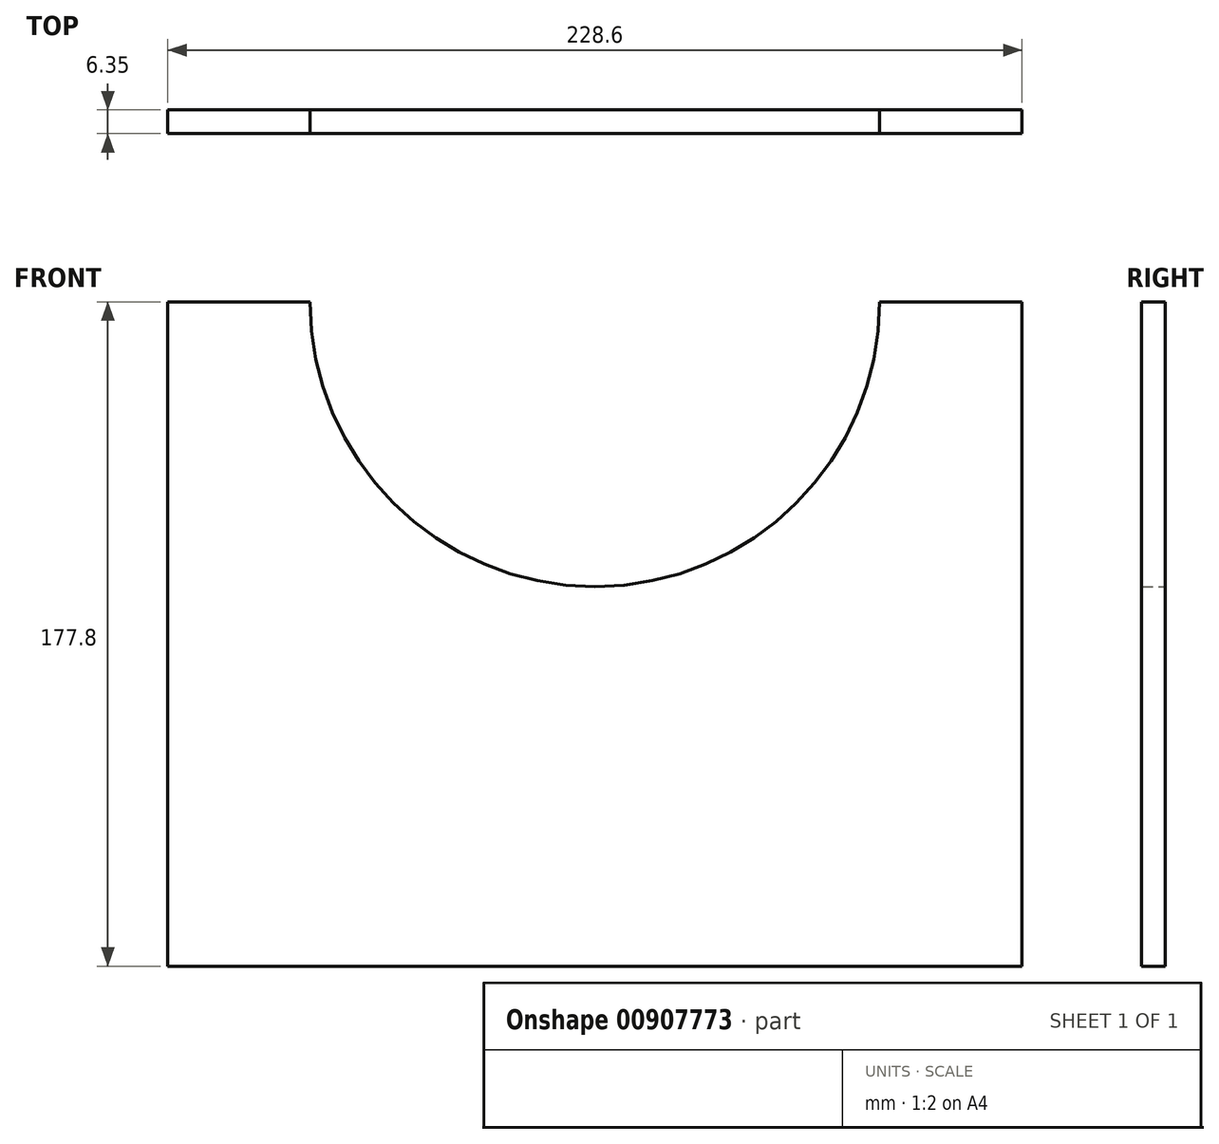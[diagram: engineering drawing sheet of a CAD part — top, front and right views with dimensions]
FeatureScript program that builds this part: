
annotation { "Feature Type Name" : "Feature", "Feature Type Description" : "" }
export const myFeature = defineFeature(function(context is Context, id is Id, definition is map)
    precondition{}
    {
        {
            var Q0;
            Q0=qCreatedBy(makeId("Front.planeOp"),FACE);
            var sketch = newSketch(context, id + "F0", { "sketchPlane" : qUnion([Q0])});
            skLineSegment(sketch, "E0.bottom", {"start": v(114.3, -88.9) * mm, "end": v(-114.3, -88.9) * mm});
            skLineSegment(sketch, "E0.top", {"start": v(114.3, 88.9) * mm, "end": v(76.2, 88.9) * mm});
            skLineSegment(sketch, "E0.left", {"start": v(114.3, -88.9) * mm, "end": v(114.3, 88.9) * mm});
            skLineSegment(sketch, "E0.right", {"start": v(-114.3, -88.9) * mm, "end": v(-114.3, 88.9) * mm});
            skPoint(sketch, "E0.middle", {"position": v(0, 0) * mm});
            skArc(sketch, "E1", {"start": v(-76.2, 88.9) * mm, "mid": v(0, 12.7) * mm, "end": v(76.2, 88.9) * mm});
            skLineSegment(sketch, "E2.trimOffspring", {"start": v(-76.2, 88.9) * mm, "end": v(-114.3, 88.9) * mm});
            skSolve(sketch);
        }
        {
            var Q0;
            Q0=makeQuery(id+"F0.imprint","IMPRINT",FACE,{"disambiguationData":[TD([[makeQuery(id+"F0.imprint","IMPRINT",EDGE,{"derivedFrom":sQuery(id+"F0.wireOp",EDGE,"E0.bottom")}),-1.0]])]});
            extrude(context, id + "F1", {"entities" : qUnion([Q0]), "depth" : 6.35 * mm, "offsetDistance" : 25.4 * mm});
        }
    });
